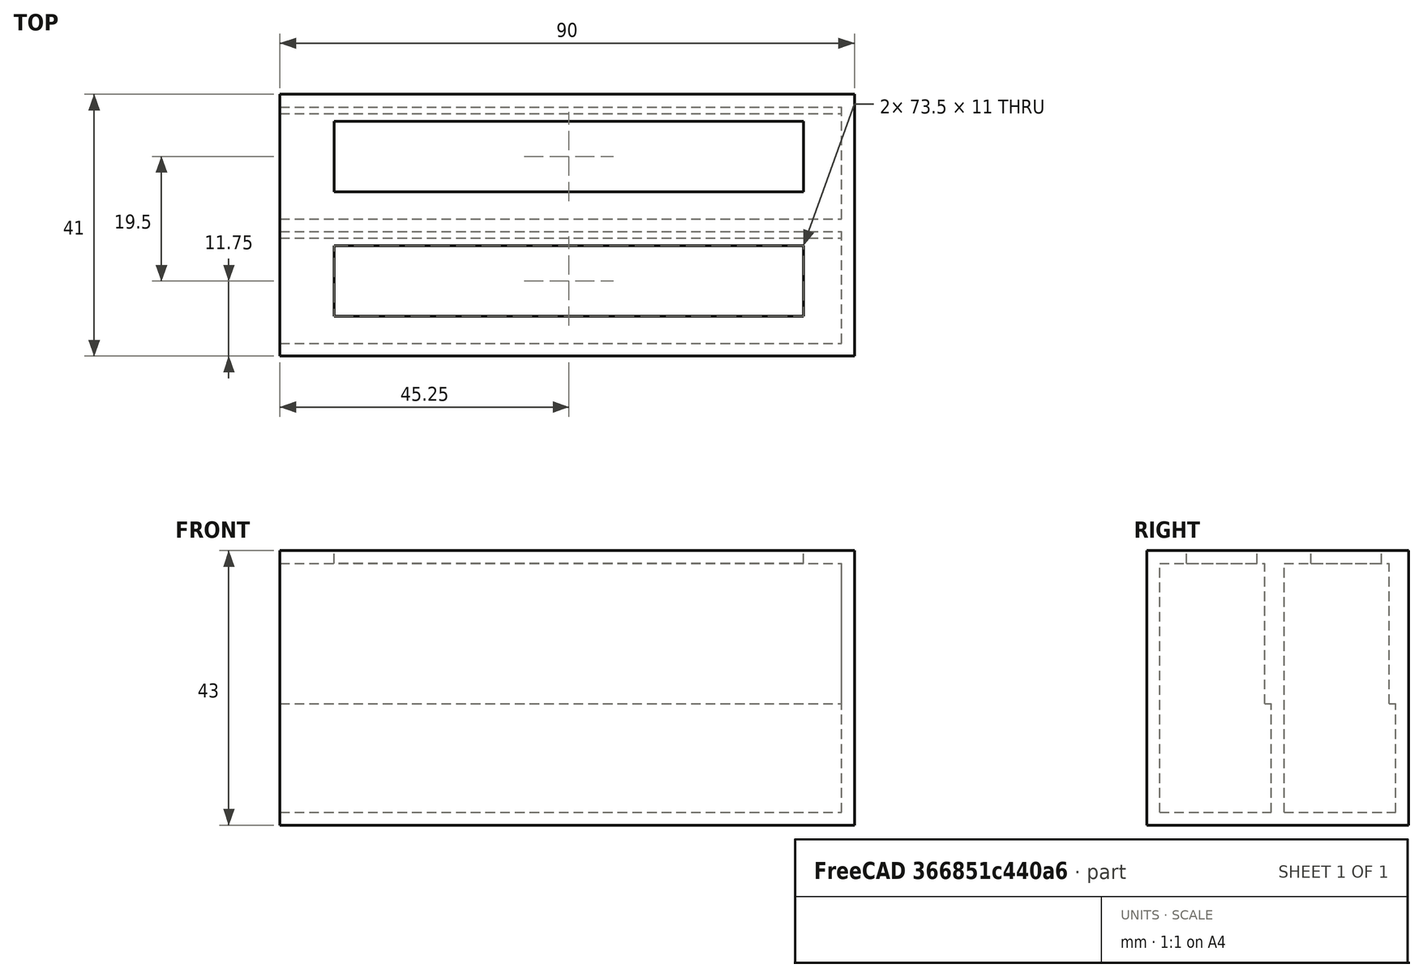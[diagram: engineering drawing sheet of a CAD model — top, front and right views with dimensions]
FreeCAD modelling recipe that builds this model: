
FCSTD DOCUMENT  (FreeCAD 0.16R6707 (Git))
Label: USB-HubHolder2
License: All rights reserved
LicenseURL: http://en.wikipedia.org/wiki/All_rights_reserved
objects: Part::Box×7, Part::Cut×6
note: 13 computed .brp shape members not serialized (recipe doc carries the construction recipe); baked Part::Feature solids carry a one-line shape summary decoded from their .brp

FEATURE [Part::Box] Box  label="Cube"
  Height = 43
  Length = 90
  Width = 41
FEATURE [Part::Box] Box001  label="Cube001"
  Height = 39
  Length = 88
  Placement = pos=(0,2,2) rot=(0,0,1;0rad)
  Width = 16.5
FEATURE [Part::Box] Box002  label="Cube002"
  Height = 39
  Length = 88
  Placement = pos=(0,21.5,2) rot=(0,0,1;0rad)
  Width = 16.5
FEATURE [Part::Cut] Cut
  Base = -> Box
  Tool = -> Box001
FEATURE [Part::Cut] Cut001
  Base = -> Cut
  Tool = -> Box002
FEATURE [Part::Box] Box003  label="Cube003"
  Height = 17
  Length = 88
  Placement = pos=(0,18.5,2) rot=(0,0,1;0rad)
  Width = 1
FEATURE [Part::Box] Box004  label="Cube004"
  Height = 17
  Length = 88
  Placement = pos=(0,38,2) rot=(0,0,1;0rad)
  Width = 1
FEATURE [Part::Cut] Cut002
  Base = -> Cut001
  Tool = -> Box003
FEATURE [Part::Cut] Cut003
  Base = -> Cut002
  Tool = -> Box004
FEATURE [Part::Box] Box005  label="Cube005"
  Height = 10
  Length = 73.5
  Placement = pos=(8.5,6.25,35) rot=(0,0,1;0rad)
  Width = 11
FEATURE [Part::Box] Box006  label="Cube006"
  Height = 10
  Length = 73.5
  Placement = pos=(8.5,25.75,35) rot=(0,0,1;0rad)
  Width = 11
FEATURE [Part::Cut] Cut004
  Base = -> Cut003
  Tool = -> Box005
FEATURE [Part::Cut] Cut005
  Base = -> Cut004
  Tool = -> Box006
